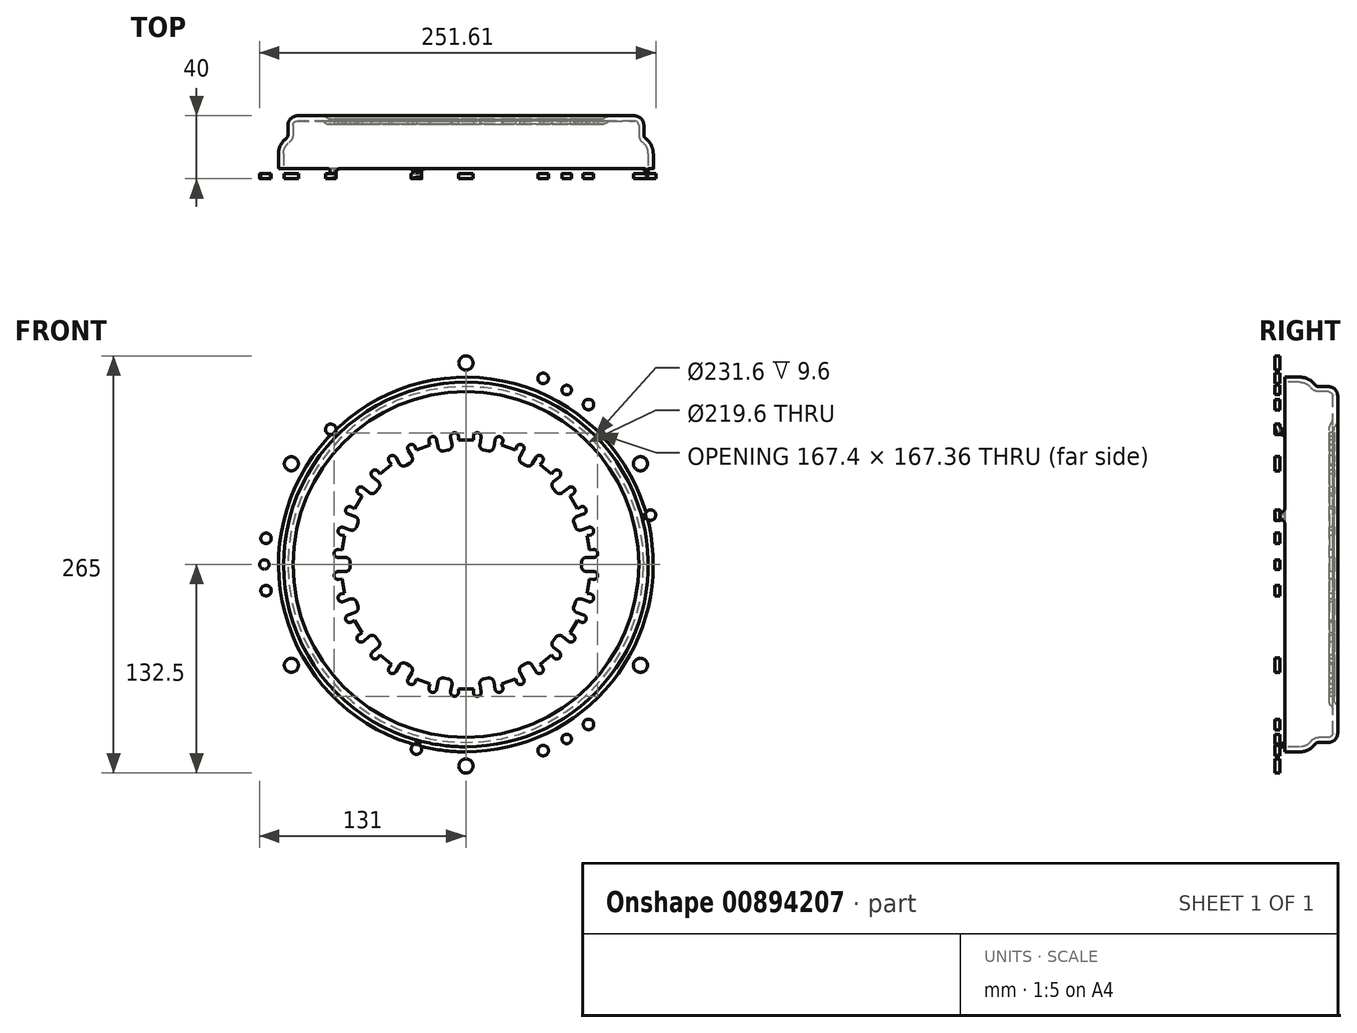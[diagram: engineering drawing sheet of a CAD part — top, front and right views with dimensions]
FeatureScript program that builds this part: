
annotation { "Feature Type Name" : "Feature", "Feature Type Description" : "" }
export const myFeature = defineFeature(function(context is Context, id is Id, definition is map)
    precondition{}
    {
        {
            var Q0;
            Q0=qCreatedBy(makeId("Right.planeOp"),FACE);
            var sketch = newSketch(context, id + "F0", { "sketchPlane" : qUnion([Q0])});
            skLineSegment(sketch, "E0", {"start": v(0, 136.5) * mm, "end": v(3.2, 136.5) * mm});
            skLineSegment(sketch, "E1", {"start": v(3.2, 136.5) * mm, "end": v(3.2, 121.5) * mm});
            skArc(sketch, "E2", {"start": v(3.2, 121.5) * mm, "mid": v(3.93, 119.73) * mm, "end": v(5.7, 119) * mm});
            skLineSegment(sketch, "E3", {"start": v(5.7, 119) * mm, "end": v(16, 119) * mm});
            skLineSegment(sketch, "E4", {"start": v(40, 107) * mm, "end": v(40, 91.97) * mm});
            skArc(sketch, "E5", {"start": v(38.15, 87.64) * mm, "mid": v(39.52, 89.62) * mm, "end": v(40, 91.97) * mm});
            skArc(sketch, "E6", {"start": v(38.15, 87.64) * mm, "mid": v(38.04, 87.48) * mm, "end": v(38, 87.28) * mm});
            skLineSegment(sketch, "E7", {"start": v(38, 87.28) * mm, "end": v(38, 73.5) * mm});
            skLineSegment(sketch, "E8", {"start": v(38, 73.5) * mm, "end": v(34.8, 73.5) * mm});
            skLineSegment(sketch, "E9", {"start": v(34, 113) * mm, "end": v(28, 113) * mm});
            skArc(sketch, "E10", {"start": v(40, 107) * mm, "mid": v(38.24, 111.24) * mm, "end": v(34, 113) * mm});
            skArc(sketch, "E11", {"start": v(25.6, 114.2) * mm, "mid": v(26.66, 113.32) * mm, "end": v(28, 113) * mm});
            skArc(sketch, "E12", {"start": v(25.6, 114.2) * mm, "mid": v(21.37, 117.73) * mm, "end": v(16, 119) * mm});
            skLineSegment(sketch, "E13", {"start": v(34.8, 73.5) * mm, "end": v(34.8, 87.28) * mm});
            skArc(sketch, "E14", {"start": v(35.94, 89.95) * mm, "mid": v(35.1, 88.73) * mm, "end": v(34.8, 87.28) * mm});
            skArc(sketch, "E15", {"start": v(35.94, 89.95) * mm, "mid": v(36.58, 90.87) * mm, "end": v(36.8, 91.97) * mm});
            skLineSegment(sketch, "E16", {"start": v(36.8, 91.97) * mm, "end": v(36.8, 107) * mm});
            skArc(sketch, "E17", {"start": v(36.8, 107) * mm, "mid": v(35.98, 108.98) * mm, "end": v(34, 109.8) * mm});
            skLineSegment(sketch, "E18", {"start": v(34, 109.8) * mm, "end": v(28, 109.8) * mm});
            skArc(sketch, "E19", {"start": v(23.04, 112.28) * mm, "mid": v(25.23, 110.45) * mm, "end": v(28, 109.8) * mm});
            skArc(sketch, "E20", {"start": v(23.04, 112.28) * mm, "mid": v(19.94, 114.87) * mm, "end": v(16, 115.8) * mm});
            skLineSegment(sketch, "E21", {"start": v(16, 115.8) * mm, "end": v(5.7, 115.8) * mm});
            skArc(sketch, "E22", {"start": v(0, 121.5) * mm, "mid": v(1.67, 117.47) * mm, "end": v(5.7, 115.8) * mm});
            skLineSegment(sketch, "E23", {"start": v(0, 0) * mm, "end": v(40, 0) * mm});
            skLineSegment(sketch, "E24", {"start": v(0, 136.5) * mm, "end": v(0, 121.5) * mm});
            skLineSegment(sketch, "E25", {"start": v(0, 121.5) * mm, "end": v(0, 0) * mm, "construction": true});
            skSolve(sketch);
        }
        {
            var Q0;
            Q0=makeQuery(id+"F0.imprint","IMPRINT",FACE,{"disambiguationData":[TD([[makeQuery(id+"F0.imprint","IMPRINT",EDGE,{"derivedFrom":sQuery(id+"F0.wireOp",EDGE,"E0")}),-1.0]])]});
            var Q1;
            Q1=sQuery(id+"F0.wireOp",EDGE,"E23");
            revolve(context, id + "F1", {"surfaceOperationType" : NewSurfaceOperationType.NEW, "entities" : qUnion([Q0]), "axis" : qUnion([Q1]), "revolveType" : RevolveType.FULL});
        }
        {
            var Q0;
            Q0=makeQuery(id+"F1.opRevolve","SWEPT_FACE",FACE,{"disambiguationData":[OSD([sQuery(id+"F0.wireOp",EDGE,"E24")])]});
            var sketch = newSketch(context, id + "F2", { "sketchPlane" : qUnion([Q0])});
            skLineSegment(sketch, "E26", {"start": v(18.53, 79.2) * mm, "end": v(17.72, 74.56) * mm});
            skArc(sketch, "E27", {"start": v(14.24, 72.12) * mm, "mid": v(16.48, 72.62) * mm, "end": v(17.72, 74.56) * mm});
            skLineSegment(sketch, "E28", {"start": v(9.67, 80.76) * mm, "end": v(8.85, 76.12) * mm});
            skLineSegment(sketch, "E29", {"start": v(12.76, 72.38) * mm, "end": v(14.24, 72.12) * mm});
            skLineSegment(sketch, "E30", {"start": v(12.76, 72.38) * mm, "end": v(11.29, 72.64) * mm});
            skArc(sketch, "E31", {"start": v(8.85, 76.12) * mm, "mid": v(9.35, 73.88) * mm, "end": v(11.29, 72.64) * mm});
            skLineSegment(sketch, "E32", {"start": v(4.7, 81.19) * mm, "end": v(4.7, 79) * mm});
            skLineSegment(sketch, "E33", {"start": v(0, 79) * mm, "end": v(4.7, 79) * mm});
            skLineSegment(sketch, "E34", {"start": v(23.34, 77.9) * mm, "end": v(22.6, 75.85) * mm});
            skLineSegment(sketch, "E35", {"start": v(27.02, 74.24) * mm, "end": v(22.6, 75.85) * mm});
            skArc(sketch, "E36", {"start": v(9.67, 80.76) * mm, "mid": v(7.43, 83.68) * mm, "end": v(4.7, 81.19) * mm});
            skArc(sketch, "E37", {"start": v(23.34, 77.9) * mm, "mid": v(21.64, 81.17) * mm, "end": v(18.53, 79.2) * mm});
            skLineSegment(sketch, "E38", {"start": v(0, 0) * mm, "end": v(0, 79) * mm, "construction": true});
            skCircle(sketch, "E39", {"center": v(0, 0) * mm, "radius": 81.5 * mm, "construction": true});
            skCircle(sketch, "E40", {"center": v(0, 0) * mm, "radius": 76.51 * mm, "construction": true});
            skLineSegment(sketch, "E41.1.0", {"start": v(-27.02, 74.24) * mm, "end": v(-22.6, 75.85) * mm});
            skLineSegment(sketch, "E41.1.1", {"start": v(-23.34, 77.9) * mm, "end": v(-22.6, 75.85) * mm});
            skArc(sketch, "E41.1.2", {"start": v(-18.53, 79.2) * mm, "mid": v(-21.64, 81.17) * mm, "end": v(-23.34, 77.9) * mm});
            skLineSegment(sketch, "E41.1.3", {"start": v(-18.53, 79.2) * mm, "end": v(-17.72, 74.56) * mm});
            skArc(sketch, "E41.1.4", {"start": v(-17.72, 74.56) * mm, "mid": v(-16.48, 72.62) * mm, "end": v(-14.24, 72.12) * mm});
            skLineSegment(sketch, "E41.1.5", {"start": v(-12.76, 72.38) * mm, "end": v(-14.24, 72.12) * mm});
            skLineSegment(sketch, "E41.1.6", {"start": v(-12.76, 72.38) * mm, "end": v(-11.29, 72.64) * mm});
            skArc(sketch, "E41.1.7", {"start": v(-11.29, 72.64) * mm, "mid": v(-9.35, 73.88) * mm, "end": v(-8.85, 76.12) * mm});
            skLineSegment(sketch, "E41.1.8", {"start": v(-9.67, 80.76) * mm, "end": v(-8.85, 76.12) * mm});
            skArc(sketch, "E41.1.9", {"start": v(-4.7, 81.19) * mm, "mid": v(-7.43, 83.68) * mm, "end": v(-9.67, 80.76) * mm});
            skLineSegment(sketch, "E41.1.10", {"start": v(-4.7, 81.19) * mm, "end": v(-4.7, 79) * mm});
            skLineSegment(sketch, "E41.1.11", {"start": v(0, 79) * mm, "end": v(-4.7, 79) * mm});
            skLineSegment(sketch, "E41.2.0", {"start": v(-50.78, 60.52) * mm, "end": v(-47.17, 63.54) * mm});
            skLineSegment(sketch, "E41.2.1", {"start": v(-48.58, 65.22) * mm, "end": v(-47.17, 63.54) * mm});
            skArc(sketch, "E41.2.2", {"start": v(-44.5, 68.08) * mm, "mid": v(-48.1, 68.88) * mm, "end": v(-48.58, 65.22) * mm});
            skLineSegment(sketch, "E41.2.3", {"start": v(-44.5, 68.08) * mm, "end": v(-42.15, 64) * mm});
            skArc(sketch, "E41.2.4", {"start": v(-42.15, 64) * mm, "mid": v(-40.33, 62.6) * mm, "end": v(-38.05, 62.9) * mm});
            skLineSegment(sketch, "E41.2.5", {"start": v(-36.75, 63.65) * mm, "end": v(-38.05, 62.9) * mm});
            skLineSegment(sketch, "E41.2.6", {"start": v(-36.75, 63.65) * mm, "end": v(-35.45, 64.4) * mm});
            skArc(sketch, "E41.2.7", {"start": v(-35.45, 64.4) * mm, "mid": v(-34.05, 66.22) * mm, "end": v(-34.35, 68.5) * mm});
            skLineSegment(sketch, "E41.2.8", {"start": v(-36.7, 72.58) * mm, "end": v(-34.35, 68.5) * mm});
            skArc(sketch, "E41.2.9", {"start": v(-32.2, 74.68) * mm, "mid": v(-35.6, 76.1) * mm, "end": v(-36.7, 72.58) * mm});
            skLineSegment(sketch, "E41.2.10", {"start": v(-32.2, 74.68) * mm, "end": v(-31.44, 72.63) * mm});
            skLineSegment(sketch, "E41.2.11", {"start": v(-27.02, 74.24) * mm, "end": v(-31.44, 72.63) * mm});
            skLineSegment(sketch, "E41.3.0", {"start": v(-68.42, 39.5) * mm, "end": v(-66.06, 43.58) * mm});
            skLineSegment(sketch, "E41.3.1", {"start": v(-67.96, 44.67) * mm, "end": v(-66.06, 43.58) * mm});
            skArc(sketch, "E41.3.2", {"start": v(-65.1, 48.75) * mm, "mid": v(-68.76, 48.27) * mm, "end": v(-67.96, 44.67) * mm});
            skLineSegment(sketch, "E41.3.3", {"start": v(-65.1, 48.75) * mm, "end": v(-61.5, 45.73) * mm});
            skArc(sketch, "E41.3.4", {"start": v(-61.5, 45.73) * mm, "mid": v(-59.3, 45.04) * mm, "end": v(-57.27, 46.1) * mm});
            skLineSegment(sketch, "E41.3.5", {"start": v(-56.3, 47.24) * mm, "end": v(-57.27, 46.1) * mm});
            skLineSegment(sketch, "E41.3.6", {"start": v(-56.3, 47.24) * mm, "end": v(-55.34, 48.4) * mm});
            skArc(sketch, "E41.3.7", {"start": v(-55.34, 48.4) * mm, "mid": v(-54.65, 50.58) * mm, "end": v(-55.7, 52.62) * mm});
            skLineSegment(sketch, "E41.3.8", {"start": v(-59.32, 55.65) * mm, "end": v(-55.7, 52.62) * mm});
            skArc(sketch, "E41.3.9", {"start": v(-55.8, 59.17) * mm, "mid": v(-59.48, 59.33) * mm, "end": v(-59.32, 55.65) * mm});
            skLineSegment(sketch, "E41.3.10", {"start": v(-55.8, 59.17) * mm, "end": v(-54.39, 57.5) * mm});
            skLineSegment(sketch, "E41.3.11", {"start": v(-50.78, 60.52) * mm, "end": v(-54.39, 57.5) * mm});
            skLineSegment(sketch, "E41.4.0", {"start": v(-77.8, 13.72) * mm, "end": v(-76.98, 18.35) * mm});
            skLineSegment(sketch, "E41.4.1", {"start": v(-79.14, 18.73) * mm, "end": v(-76.98, 18.35) * mm});
            skArc(sketch, "E41.4.2", {"start": v(-77.85, 23.55) * mm, "mid": v(-81.12, 21.84) * mm, "end": v(-79.14, 18.73) * mm});
            skLineSegment(sketch, "E41.4.3", {"start": v(-77.85, 23.55) * mm, "end": v(-73.43, 21.94) * mm});
            skArc(sketch, "E41.4.4", {"start": v(-73.43, 21.94) * mm, "mid": v(-71.13, 22.04) * mm, "end": v(-69.58, 23.73) * mm});
            skLineSegment(sketch, "E41.4.5", {"start": v(-69.07, 25.14) * mm, "end": v(-69.58, 23.73) * mm});
            skLineSegment(sketch, "E41.4.6", {"start": v(-69.07, 25.14) * mm, "end": v(-68.55, 26.55) * mm});
            skArc(sketch, "E41.4.7", {"start": v(-68.55, 26.55) * mm, "mid": v(-68.65, 28.84) * mm, "end": v(-70.35, 30.4) * mm});
            skLineSegment(sketch, "E41.4.8", {"start": v(-74.77, 32) * mm, "end": v(-70.35, 30.4) * mm});
            skArc(sketch, "E41.4.9", {"start": v(-72.67, 36.52) * mm, "mid": v(-76.18, 35.4) * mm, "end": v(-74.77, 32) * mm});
            skLineSegment(sketch, "E41.4.10", {"start": v(-72.67, 36.52) * mm, "end": v(-70.77, 35.42) * mm});
            skLineSegment(sketch, "E41.4.11", {"start": v(-68.42, 39.5) * mm, "end": v(-70.77, 35.42) * mm});
            skLineSegment(sketch, "E41.5.0", {"start": v(-77.8, -13.72) * mm, "end": v(-78.62, -9.08) * mm});
            skLineSegment(sketch, "E41.5.1", {"start": v(-80.77, -9.46) * mm, "end": v(-78.62, -9.08) * mm});
            skArc(sketch, "E41.5.2", {"start": v(-81.2, -4.5) * mm, "mid": v(-83.7, -7.22) * mm, "end": v(-80.77, -9.46) * mm});
            skLineSegment(sketch, "E41.5.3", {"start": v(-81.2, -4.5) * mm, "end": v(-76.5, -4.5) * mm});
            skArc(sketch, "E41.5.4", {"start": v(-76.5, -4.5) * mm, "mid": v(-74.38, -3.62) * mm, "end": v(-73.5, -1.5) * mm});
            skLineSegment(sketch, "E41.5.5", {"start": v(-73.5, 0) * mm, "end": v(-73.5, -1.5) * mm});
            skLineSegment(sketch, "E41.5.6", {"start": v(-73.5, 0) * mm, "end": v(-73.5, 1.5) * mm});
            skArc(sketch, "E41.5.7", {"start": v(-73.5, 1.5) * mm, "mid": v(-74.38, 3.62) * mm, "end": v(-76.5, 4.5) * mm});
            skLineSegment(sketch, "E41.5.8", {"start": v(-81.2, 4.5) * mm, "end": v(-76.5, 4.5) * mm});
            skArc(sketch, "E41.5.9", {"start": v(-80.77, 9.46) * mm, "mid": v(-83.7, 7.22) * mm, "end": v(-81.2, 4.5) * mm});
            skLineSegment(sketch, "E41.5.10", {"start": v(-80.77, 9.46) * mm, "end": v(-78.62, 9.08) * mm});
            skLineSegment(sketch, "E41.5.11", {"start": v(-77.8, 13.72) * mm, "end": v(-78.62, 9.08) * mm});
            skLineSegment(sketch, "E41.6.0", {"start": v(-68.42, -39.5) * mm, "end": v(-70.77, -35.42) * mm});
            skLineSegment(sketch, "E41.6.1", {"start": v(-72.67, -36.52) * mm, "end": v(-70.77, -35.42) * mm});
            skArc(sketch, "E41.6.2", {"start": v(-74.77, -32) * mm, "mid": v(-76.18, -35.4) * mm, "end": v(-72.67, -36.52) * mm});
            skLineSegment(sketch, "E41.6.3", {"start": v(-74.77, -32) * mm, "end": v(-70.35, -30.4) * mm});
            skArc(sketch, "E41.6.4", {"start": v(-70.35, -30.4) * mm, "mid": v(-68.65, -28.84) * mm, "end": v(-68.55, -26.55) * mm});
            skLineSegment(sketch, "E41.6.5", {"start": v(-69.07, -25.14) * mm, "end": v(-68.55, -26.55) * mm});
            skLineSegment(sketch, "E41.6.6", {"start": v(-69.07, -25.14) * mm, "end": v(-69.58, -23.73) * mm});
            skArc(sketch, "E41.6.7", {"start": v(-69.58, -23.73) * mm, "mid": v(-71.13, -22.04) * mm, "end": v(-73.43, -21.94) * mm});
            skLineSegment(sketch, "E41.6.8", {"start": v(-77.85, -23.55) * mm, "end": v(-73.43, -21.94) * mm});
            skArc(sketch, "E41.6.9", {"start": v(-79.14, -18.73) * mm, "mid": v(-81.12, -21.84) * mm, "end": v(-77.85, -23.55) * mm});
            skLineSegment(sketch, "E41.6.10", {"start": v(-79.14, -18.73) * mm, "end": v(-76.98, -18.35) * mm});
            skLineSegment(sketch, "E41.6.11", {"start": v(-77.8, -13.72) * mm, "end": v(-76.98, -18.35) * mm});
            skLineSegment(sketch, "E41.7.0", {"start": v(-50.78, -60.52) * mm, "end": v(-54.39, -57.5) * mm});
            skLineSegment(sketch, "E41.7.1", {"start": v(-55.8, -59.17) * mm, "end": v(-54.39, -57.5) * mm});
            skArc(sketch, "E41.7.2", {"start": v(-59.32, -55.65) * mm, "mid": v(-59.48, -59.33) * mm, "end": v(-55.8, -59.17) * mm});
            skLineSegment(sketch, "E41.7.3", {"start": v(-59.32, -55.65) * mm, "end": v(-55.7, -52.62) * mm});
            skArc(sketch, "E41.7.4", {"start": v(-55.7, -52.62) * mm, "mid": v(-54.65, -50.58) * mm, "end": v(-55.34, -48.4) * mm});
            skLineSegment(sketch, "E41.7.5", {"start": v(-56.3, -47.24) * mm, "end": v(-55.34, -48.4) * mm});
            skLineSegment(sketch, "E41.7.6", {"start": v(-56.3, -47.24) * mm, "end": v(-57.27, -46.1) * mm});
            skArc(sketch, "E41.7.7", {"start": v(-57.27, -46.1) * mm, "mid": v(-59.3, -45.04) * mm, "end": v(-61.5, -45.73) * mm});
            skLineSegment(sketch, "E41.7.8", {"start": v(-65.1, -48.75) * mm, "end": v(-61.5, -45.73) * mm});
            skArc(sketch, "E41.7.9", {"start": v(-67.96, -44.67) * mm, "mid": v(-68.76, -48.27) * mm, "end": v(-65.1, -48.75) * mm});
            skLineSegment(sketch, "E41.7.10", {"start": v(-67.96, -44.67) * mm, "end": v(-66.06, -43.58) * mm});
            skLineSegment(sketch, "E41.7.11", {"start": v(-68.42, -39.5) * mm, "end": v(-66.06, -43.58) * mm});
            skLineSegment(sketch, "E41.8.0", {"start": v(-27.02, -74.24) * mm, "end": v(-31.44, -72.63) * mm});
            skLineSegment(sketch, "E41.8.1", {"start": v(-32.2, -74.68) * mm, "end": v(-31.44, -72.63) * mm});
            skArc(sketch, "E41.8.2", {"start": v(-36.7, -72.58) * mm, "mid": v(-35.6, -76.1) * mm, "end": v(-32.2, -74.68) * mm});
            skLineSegment(sketch, "E41.8.3", {"start": v(-36.7, -72.58) * mm, "end": v(-34.35, -68.5) * mm});
            skArc(sketch, "E41.8.4", {"start": v(-34.35, -68.5) * mm, "mid": v(-34.05, -66.22) * mm, "end": v(-35.45, -64.4) * mm});
            skLineSegment(sketch, "E41.8.5", {"start": v(-36.75, -63.65) * mm, "end": v(-35.45, -64.4) * mm});
            skLineSegment(sketch, "E41.8.6", {"start": v(-36.75, -63.65) * mm, "end": v(-38.05, -62.9) * mm});
            skArc(sketch, "E41.8.7", {"start": v(-38.05, -62.9) * mm, "mid": v(-40.33, -62.6) * mm, "end": v(-42.15, -64) * mm});
            skLineSegment(sketch, "E41.8.8", {"start": v(-44.5, -68.08) * mm, "end": v(-42.15, -64) * mm});
            skArc(sketch, "E41.8.9", {"start": v(-48.58, -65.22) * mm, "mid": v(-48.1, -68.88) * mm, "end": v(-44.5, -68.08) * mm});
            skLineSegment(sketch, "E41.8.10", {"start": v(-48.58, -65.22) * mm, "end": v(-47.17, -63.54) * mm});
            skLineSegment(sketch, "E41.8.11", {"start": v(-50.78, -60.52) * mm, "end": v(-47.17, -63.54) * mm});
            skLineSegment(sketch, "E41.9.0", {"start": v(0, -79) * mm, "end": v(-4.7, -79) * mm});
            skLineSegment(sketch, "E41.9.1", {"start": v(-4.7, -81.19) * mm, "end": v(-4.7, -79) * mm});
            skArc(sketch, "E41.9.2", {"start": v(-9.67, -80.76) * mm, "mid": v(-7.43, -83.68) * mm, "end": v(-4.7, -81.19) * mm});
            skLineSegment(sketch, "E41.9.3", {"start": v(-9.67, -80.76) * mm, "end": v(-8.85, -76.12) * mm});
            skArc(sketch, "E41.9.4", {"start": v(-8.85, -76.12) * mm, "mid": v(-9.35, -73.88) * mm, "end": v(-11.29, -72.64) * mm});
            skLineSegment(sketch, "E41.9.5", {"start": v(-12.76, -72.38) * mm, "end": v(-11.29, -72.64) * mm});
            skLineSegment(sketch, "E41.9.6", {"start": v(-12.76, -72.38) * mm, "end": v(-14.24, -72.12) * mm});
            skArc(sketch, "E41.9.7", {"start": v(-14.24, -72.12) * mm, "mid": v(-16.48, -72.62) * mm, "end": v(-17.72, -74.56) * mm});
            skLineSegment(sketch, "E41.9.8", {"start": v(-18.53, -79.2) * mm, "end": v(-17.72, -74.56) * mm});
            skArc(sketch, "E41.9.9", {"start": v(-23.34, -77.9) * mm, "mid": v(-21.64, -81.17) * mm, "end": v(-18.53, -79.2) * mm});
            skLineSegment(sketch, "E41.9.10", {"start": v(-23.34, -77.9) * mm, "end": v(-22.6, -75.85) * mm});
            skLineSegment(sketch, "E41.9.11", {"start": v(-27.02, -74.24) * mm, "end": v(-22.6, -75.85) * mm});
            skLineSegment(sketch, "E41.10.0", {"start": v(27.02, -74.24) * mm, "end": v(22.6, -75.85) * mm});
            skLineSegment(sketch, "E41.10.1", {"start": v(23.34, -77.9) * mm, "end": v(22.6, -75.85) * mm});
            skArc(sketch, "E41.10.2", {"start": v(18.53, -79.2) * mm, "mid": v(21.64, -81.17) * mm, "end": v(23.34, -77.9) * mm});
            skLineSegment(sketch, "E41.10.3", {"start": v(18.53, -79.2) * mm, "end": v(17.72, -74.56) * mm});
            skArc(sketch, "E41.10.4", {"start": v(17.72, -74.56) * mm, "mid": v(16.48, -72.62) * mm, "end": v(14.24, -72.12) * mm});
            skLineSegment(sketch, "E41.10.5", {"start": v(12.76, -72.38) * mm, "end": v(14.24, -72.12) * mm});
            skLineSegment(sketch, "E41.10.6", {"start": v(12.76, -72.38) * mm, "end": v(11.29, -72.64) * mm});
            skArc(sketch, "E41.10.7", {"start": v(11.29, -72.64) * mm, "mid": v(9.35, -73.88) * mm, "end": v(8.85, -76.12) * mm});
            skLineSegment(sketch, "E41.10.8", {"start": v(9.67, -80.76) * mm, "end": v(8.85, -76.12) * mm});
            skArc(sketch, "E41.10.9", {"start": v(4.7, -81.19) * mm, "mid": v(7.43, -83.68) * mm, "end": v(9.67, -80.76) * mm});
            skLineSegment(sketch, "E41.10.10", {"start": v(4.7, -81.19) * mm, "end": v(4.7, -79) * mm});
            skLineSegment(sketch, "E41.10.11", {"start": v(0, -79) * mm, "end": v(4.7, -79) * mm});
            skLineSegment(sketch, "E41.11.0", {"start": v(50.78, -60.52) * mm, "end": v(47.17, -63.54) * mm});
            skLineSegment(sketch, "E41.11.1", {"start": v(48.58, -65.22) * mm, "end": v(47.17, -63.54) * mm});
            skArc(sketch, "E41.11.2", {"start": v(44.5, -68.08) * mm, "mid": v(48.1, -68.88) * mm, "end": v(48.58, -65.22) * mm});
            skLineSegment(sketch, "E41.11.3", {"start": v(44.5, -68.08) * mm, "end": v(42.15, -64) * mm});
            skArc(sketch, "E41.11.4", {"start": v(42.15, -64) * mm, "mid": v(40.33, -62.6) * mm, "end": v(38.05, -62.9) * mm});
            skLineSegment(sketch, "E41.11.5", {"start": v(36.75, -63.65) * mm, "end": v(38.05, -62.9) * mm});
            skLineSegment(sketch, "E41.11.6", {"start": v(36.75, -63.65) * mm, "end": v(35.45, -64.4) * mm});
            skArc(sketch, "E41.11.7", {"start": v(35.45, -64.4) * mm, "mid": v(34.05, -66.22) * mm, "end": v(34.35, -68.5) * mm});
            skLineSegment(sketch, "E41.11.8", {"start": v(36.7, -72.58) * mm, "end": v(34.35, -68.5) * mm});
            skArc(sketch, "E41.11.9", {"start": v(32.2, -74.68) * mm, "mid": v(35.6, -76.1) * mm, "end": v(36.7, -72.58) * mm});
            skLineSegment(sketch, "E41.11.10", {"start": v(32.2, -74.68) * mm, "end": v(31.44, -72.63) * mm});
            skLineSegment(sketch, "E41.11.11", {"start": v(27.02, -74.24) * mm, "end": v(31.44, -72.63) * mm});
            skLineSegment(sketch, "E41.12.0", {"start": v(68.42, -39.5) * mm, "end": v(66.06, -43.58) * mm});
            skLineSegment(sketch, "E41.12.1", {"start": v(67.96, -44.67) * mm, "end": v(66.06, -43.58) * mm});
            skArc(sketch, "E41.12.2", {"start": v(65.1, -48.75) * mm, "mid": v(68.76, -48.27) * mm, "end": v(67.96, -44.67) * mm});
            skLineSegment(sketch, "E41.12.3", {"start": v(65.1, -48.75) * mm, "end": v(61.5, -45.73) * mm});
            skArc(sketch, "E41.12.4", {"start": v(61.5, -45.73) * mm, "mid": v(59.3, -45.04) * mm, "end": v(57.27, -46.1) * mm});
            skLineSegment(sketch, "E41.12.5", {"start": v(56.3, -47.24) * mm, "end": v(57.27, -46.1) * mm});
            skLineSegment(sketch, "E41.12.6", {"start": v(56.3, -47.24) * mm, "end": v(55.34, -48.4) * mm});
            skArc(sketch, "E41.12.7", {"start": v(55.34, -48.4) * mm, "mid": v(54.65, -50.58) * mm, "end": v(55.7, -52.62) * mm});
            skLineSegment(sketch, "E41.12.8", {"start": v(59.32, -55.65) * mm, "end": v(55.7, -52.62) * mm});
            skArc(sketch, "E41.12.9", {"start": v(55.8, -59.17) * mm, "mid": v(59.48, -59.33) * mm, "end": v(59.32, -55.65) * mm});
            skLineSegment(sketch, "E41.12.10", {"start": v(55.8, -59.17) * mm, "end": v(54.39, -57.5) * mm});
            skLineSegment(sketch, "E41.12.11", {"start": v(50.78, -60.52) * mm, "end": v(54.39, -57.5) * mm});
            skLineSegment(sketch, "E41.13.0", {"start": v(77.8, -13.72) * mm, "end": v(76.98, -18.35) * mm});
            skLineSegment(sketch, "E41.13.1", {"start": v(79.14, -18.73) * mm, "end": v(76.98, -18.35) * mm});
            skArc(sketch, "E41.13.2", {"start": v(77.85, -23.55) * mm, "mid": v(81.12, -21.84) * mm, "end": v(79.14, -18.73) * mm});
            skLineSegment(sketch, "E41.13.3", {"start": v(77.85, -23.55) * mm, "end": v(73.43, -21.94) * mm});
            skArc(sketch, "E41.13.4", {"start": v(73.43, -21.94) * mm, "mid": v(71.13, -22.04) * mm, "end": v(69.58, -23.73) * mm});
            skLineSegment(sketch, "E41.13.5", {"start": v(69.07, -25.14) * mm, "end": v(69.58, -23.73) * mm});
            skLineSegment(sketch, "E41.13.6", {"start": v(69.07, -25.14) * mm, "end": v(68.55, -26.55) * mm});
            skArc(sketch, "E41.13.7", {"start": v(68.55, -26.55) * mm, "mid": v(68.65, -28.84) * mm, "end": v(70.35, -30.4) * mm});
            skLineSegment(sketch, "E41.13.8", {"start": v(74.77, -32) * mm, "end": v(70.35, -30.4) * mm});
            skArc(sketch, "E41.13.9", {"start": v(72.67, -36.52) * mm, "mid": v(76.18, -35.4) * mm, "end": v(74.77, -32) * mm});
            skLineSegment(sketch, "E41.13.10", {"start": v(72.67, -36.52) * mm, "end": v(70.77, -35.42) * mm});
            skLineSegment(sketch, "E41.13.11", {"start": v(68.42, -39.5) * mm, "end": v(70.77, -35.42) * mm});
            skLineSegment(sketch, "E41.14.0", {"start": v(77.8, 13.72) * mm, "end": v(78.62, 9.08) * mm});
            skLineSegment(sketch, "E41.14.1", {"start": v(80.77, 9.46) * mm, "end": v(78.62, 9.08) * mm});
            skArc(sketch, "E41.14.2", {"start": v(81.2, 4.5) * mm, "mid": v(83.7, 7.22) * mm, "end": v(80.77, 9.46) * mm});
            skLineSegment(sketch, "E41.14.3", {"start": v(81.2, 4.5) * mm, "end": v(76.5, 4.5) * mm});
            skArc(sketch, "E41.14.4", {"start": v(76.5, 4.5) * mm, "mid": v(74.38, 3.62) * mm, "end": v(73.5, 1.5) * mm});
            skLineSegment(sketch, "E41.14.5", {"start": v(73.5, 0) * mm, "end": v(73.5, 1.5) * mm});
            skLineSegment(sketch, "E41.14.6", {"start": v(73.5, 0) * mm, "end": v(73.5, -1.5) * mm});
            skArc(sketch, "E41.14.7", {"start": v(73.5, -1.5) * mm, "mid": v(74.38, -3.62) * mm, "end": v(76.5, -4.5) * mm});
            skLineSegment(sketch, "E41.14.8", {"start": v(81.2, -4.5) * mm, "end": v(76.5, -4.5) * mm});
            skArc(sketch, "E41.14.9", {"start": v(80.77, -9.46) * mm, "mid": v(83.7, -7.22) * mm, "end": v(81.2, -4.5) * mm});
            skLineSegment(sketch, "E41.14.10", {"start": v(80.77, -9.46) * mm, "end": v(78.62, -9.08) * mm});
            skLineSegment(sketch, "E41.14.11", {"start": v(77.8, -13.72) * mm, "end": v(78.62, -9.08) * mm});
            skLineSegment(sketch, "E41.15.0", {"start": v(68.42, 39.5) * mm, "end": v(70.77, 35.42) * mm});
            skLineSegment(sketch, "E41.15.1", {"start": v(72.67, 36.52) * mm, "end": v(70.77, 35.42) * mm});
            skArc(sketch, "E41.15.2", {"start": v(74.77, 32) * mm, "mid": v(76.18, 35.4) * mm, "end": v(72.67, 36.52) * mm});
            skLineSegment(sketch, "E41.15.3", {"start": v(74.77, 32) * mm, "end": v(70.35, 30.4) * mm});
            skArc(sketch, "E41.15.4", {"start": v(70.35, 30.4) * mm, "mid": v(68.65, 28.84) * mm, "end": v(68.55, 26.55) * mm});
            skLineSegment(sketch, "E41.15.5", {"start": v(69.07, 25.14) * mm, "end": v(68.55, 26.55) * mm});
            skLineSegment(sketch, "E41.15.6", {"start": v(69.07, 25.14) * mm, "end": v(69.58, 23.73) * mm});
            skArc(sketch, "E41.15.7", {"start": v(69.58, 23.73) * mm, "mid": v(71.13, 22.04) * mm, "end": v(73.43, 21.94) * mm});
            skLineSegment(sketch, "E41.15.8", {"start": v(77.85, 23.55) * mm, "end": v(73.43, 21.94) * mm});
            skArc(sketch, "E41.15.9", {"start": v(79.14, 18.73) * mm, "mid": v(81.12, 21.84) * mm, "end": v(77.85, 23.55) * mm});
            skLineSegment(sketch, "E41.15.10", {"start": v(79.14, 18.73) * mm, "end": v(76.98, 18.35) * mm});
            skLineSegment(sketch, "E41.15.11", {"start": v(77.8, 13.72) * mm, "end": v(76.98, 18.35) * mm});
            skLineSegment(sketch, "E41.16.0", {"start": v(50.78, 60.52) * mm, "end": v(54.39, 57.5) * mm});
            skLineSegment(sketch, "E41.16.1", {"start": v(55.8, 59.17) * mm, "end": v(54.39, 57.5) * mm});
            skArc(sketch, "E41.16.2", {"start": v(59.32, 55.65) * mm, "mid": v(59.48, 59.33) * mm, "end": v(55.8, 59.17) * mm});
            skLineSegment(sketch, "E41.16.3", {"start": v(59.32, 55.65) * mm, "end": v(55.7, 52.62) * mm});
            skArc(sketch, "E41.16.4", {"start": v(55.7, 52.62) * mm, "mid": v(54.65, 50.58) * mm, "end": v(55.34, 48.4) * mm});
            skLineSegment(sketch, "E41.16.5", {"start": v(56.3, 47.24) * mm, "end": v(55.34, 48.4) * mm});
            skLineSegment(sketch, "E41.16.6", {"start": v(56.3, 47.24) * mm, "end": v(57.27, 46.1) * mm});
            skArc(sketch, "E41.16.7", {"start": v(57.27, 46.1) * mm, "mid": v(59.3, 45.04) * mm, "end": v(61.5, 45.73) * mm});
            skLineSegment(sketch, "E41.16.8", {"start": v(65.1, 48.75) * mm, "end": v(61.5, 45.73) * mm});
            skArc(sketch, "E41.16.9", {"start": v(67.96, 44.67) * mm, "mid": v(68.76, 48.27) * mm, "end": v(65.1, 48.75) * mm});
            skLineSegment(sketch, "E41.16.10", {"start": v(67.96, 44.67) * mm, "end": v(66.06, 43.58) * mm});
            skLineSegment(sketch, "E41.16.11", {"start": v(68.42, 39.5) * mm, "end": v(66.06, 43.58) * mm});
            skLineSegment(sketch, "E41.17.0", {"start": v(27.02, 74.24) * mm, "end": v(31.44, 72.63) * mm});
            skLineSegment(sketch, "E41.17.1", {"start": v(32.2, 74.68) * mm, "end": v(31.44, 72.63) * mm});
            skArc(sketch, "E41.17.2", {"start": v(36.7, 72.58) * mm, "mid": v(35.6, 76.1) * mm, "end": v(32.2, 74.68) * mm});
            skLineSegment(sketch, "E41.17.3", {"start": v(36.7, 72.58) * mm, "end": v(34.35, 68.5) * mm});
            skArc(sketch, "E41.17.4", {"start": v(34.35, 68.5) * mm, "mid": v(34.05, 66.22) * mm, "end": v(35.45, 64.4) * mm});
            skLineSegment(sketch, "E41.17.5", {"start": v(36.75, 63.65) * mm, "end": v(35.45, 64.4) * mm});
            skLineSegment(sketch, "E41.17.6", {"start": v(36.75, 63.65) * mm, "end": v(38.05, 62.9) * mm});
            skArc(sketch, "E41.17.7", {"start": v(38.05, 62.9) * mm, "mid": v(40.33, 62.6) * mm, "end": v(42.15, 64) * mm});
            skLineSegment(sketch, "E41.17.8", {"start": v(44.5, 68.08) * mm, "end": v(42.15, 64) * mm});
            skArc(sketch, "E41.17.9", {"start": v(48.58, 65.22) * mm, "mid": v(48.1, 68.88) * mm, "end": v(44.5, 68.08) * mm});
            skLineSegment(sketch, "E41.17.10", {"start": v(48.58, 65.22) * mm, "end": v(47.17, 63.54) * mm});
            skLineSegment(sketch, "E41.17.11", {"start": v(50.78, 60.52) * mm, "end": v(47.17, 63.54) * mm});
            skCircle(sketch, "E42", {"center": v(0, 0) * mm, "radius": 70 * mm});
            skSolve(sketch);
        }
        {
            var Q0;
            Q0=makeQuery(id+"F2.imprint","IMPRINT",FACE,{"disambiguationData":[TD([[makeQuery(id+"F2.imprint","IMPRINT",EDGE,{"derivedFrom":sQuery(id+"F2.wireOp",EDGE,"E26")}),1.0]])]});
            extrude(context, id + "F3", {"entities" : qUnion([Q0]), "operationType" : NewBodyOperationType.REMOVE, "endBound" : BoundingType.THROUGH_ALL, "oppositeDirection" : true, "depth" : 25 * mm, "offsetDistance" : 25 * mm});
        }
        {
            var Q0;
            Q0=makeQuery(id+"F1.opRevolve","SWEPT_FACE",FACE,{"disambiguationData":[OSD([sQuery(id+"F0.wireOp",EDGE,"E24")])]});
            var sketch = newSketch(context, id + "F4", { "sketchPlane" : qUnion([Q0])});
            skArc(sketch, "E43", {"start": v(121.35, 62.5) * mm, "mid": v(68.25, 118.21) * mm, "end": v(-6.55, 136.34) * mm});
            skCircle(sketch, "E44", {"center": v(0, 128) * mm, "radius": 4.5 * mm});
            skCircle(sketch, "E45", {"center": v(-110.85, 64) * mm, "radius": 4.5 * mm});
            skCircle(sketch, "E46", {"center": v(64, 110.85) * mm, "radius": 3 * mm});
            skCircle(sketch, "E47", {"center": v(-85.84, 85.84) * mm, "radius": 3.35 * mm});
            skArc(sketch, "E48", {"start": v(-20.8, 125.03) * mm, "mid": v(-52.53, 115.35) * mm, "end": v(-80.66, 97.77) * mm});
            skArc(sketch, "E49", {"start": v(-83.02, 98.4) * mm, "mid": v(-91.34, 90.74) * mm, "end": v(-98.95, 82.38) * mm});
            skLineSegment(sketch, "E50", {"start": v(-114.8, 73.84) * mm, "end": v(-98.95, 82.38) * mm});
            skLineSegment(sketch, "E51", {"start": v(-6.55, 136.34) * mm, "end": v(-20.8, 125.03) * mm});
            skLineSegment(sketch, "E52", {"start": v(-83.02, 98.4) * mm, "end": v(-80.66, 97.77) * mm});
            skCircle(sketch, "E53", {"center": v(49.07, 118.22) * mm, "radius": 3.35 * mm});
            skCircle(sketch, "E54", {"center": v(77.85, 101.6) * mm, "radius": 3.35 * mm});
            skLineSegment(sketch, "E55", {"start": v(0, 0) * mm, "end": v(0, 136.5) * mm, "construction": true});
            skCircle(sketch, "E56", {"center": v(0, 0) * mm, "radius": 128 * mm, "construction": true});
            skLineSegment(sketch, "E57", {"start": v(49.07, 118.22) * mm, "end": v(0, 0) * mm, "construction": true});
            skLineSegment(sketch, "E58", {"start": v(64, 110.85) * mm, "end": v(0, 0) * mm, "construction": true});
            skLineSegment(sketch, "E59", {"start": v(77.85, 101.6) * mm, "end": v(0, 0) * mm, "construction": true});
            skLineSegment(sketch, "E60", {"start": v(-85.84, 85.84) * mm, "end": v(0, 0) * mm, "construction": true});
            skLineSegment(sketch, "E61", {"start": v(-110.85, 64) * mm, "end": v(0, 0) * mm, "construction": true});
            skCircle(sketch, "E62.1.0", {"center": v(0, -128) * mm, "radius": 4.5 * mm});
            skLineSegment(sketch, "E62.1.1", {"start": v(-6.55, -136.34) * mm, "end": v(-21.87, -126.88) * mm});
            skArc(sketch, "E62.1.2", {"start": v(-43.7, -121.1) * mm, "mid": v(-32.92, -124.47) * mm, "end": v(-21.87, -126.88) * mm});
            skLineSegment(sketch, "E62.1.3", {"start": v(-43.7, -121.1) * mm, "end": v(-44.34, -118.74) * mm});
            skArc(sketch, "E62.1.4", {"start": v(-97.88, -80.53) * mm, "mid": v(-73.63, -103.17) * mm, "end": v(-44.34, -118.74) * mm});
            skLineSegment(sketch, "E62.1.5", {"start": v(-114.8, -73.84) * mm, "end": v(-97.88, -80.53) * mm});
            skArc(sketch, "E62.1.6", {"start": v(-114.8, 73.84) * mm, "mid": v(-136.5, 0) * mm, "end": v(-114.8, -73.84) * mm});
            skCircle(sketch, "E62.1.7", {"center": v(-110.85, -64) * mm, "radius": 4.5 * mm});
            skCircle(sketch, "E62.1.8", {"center": v(-31.42, -117.26) * mm, "radius": 3.35 * mm});
            skCircle(sketch, "E62.1.9", {"center": v(-126.92, -16.61) * mm, "radius": 3.35 * mm});
            skCircle(sketch, "E62.1.10", {"center": v(-128, 0) * mm, "radius": 3 * mm});
            skCircle(sketch, "E62.1.11", {"center": v(-126.92, 16.61) * mm, "radius": 3.35 * mm});
            skCircle(sketch, "E62.2.0", {"center": v(110.85, 64) * mm, "radius": 4.5 * mm});
            skLineSegment(sketch, "E62.2.1", {"start": v(121.35, 62.5) * mm, "end": v(120.82, 44.5) * mm});
            skArc(sketch, "E62.2.2", {"start": v(126.73, 22.7) * mm, "mid": v(124.25, 33.73) * mm, "end": v(120.82, 44.5) * mm});
            skLineSegment(sketch, "E62.2.3", {"start": v(126.73, 22.7) * mm, "end": v(125, 20.97) * mm});
            skArc(sketch, "E62.2.4", {"start": v(118.68, -44.5) * mm, "mid": v(126.16, -12.18) * mm, "end": v(125, 20.97) * mm});
            skLineSegment(sketch, "E62.2.5", {"start": v(121.35, -62.5) * mm, "end": v(118.68, -44.5) * mm});
            skArc(sketch, "E62.2.6", {"start": v(-6.55, -136.34) * mm, "mid": v(68.25, -118.21) * mm, "end": v(121.35, -62.5) * mm});
            skCircle(sketch, "E62.2.7", {"center": v(110.85, -64) * mm, "radius": 4.5 * mm});
            skCircle(sketch, "E62.2.8", {"center": v(117.26, 31.42) * mm, "radius": 3.35 * mm});
            skCircle(sketch, "E62.2.9", {"center": v(77.85, -101.6) * mm, "radius": 3.35 * mm});
            skCircle(sketch, "E62.2.10", {"center": v(64, -110.85) * mm, "radius": 3 * mm});
            skCircle(sketch, "E62.2.11", {"center": v(49.07, -118.22) * mm, "radius": 3.35 * mm});
            skCircle(sketch, "E63", {"center": v(0, 0) * mm, "radius": 150 * mm});
            skSolve(sketch);
        }
        {
            var Q0;
            Q0=makeQuery(id+"F4.imprint","IMPRINT",FACE,{"disambiguationData":[TD([[makeQuery(id+"F4.imprint","IMPRINT",EDGE,{"derivedFrom":sQuery(id+"F4.wireOp",EDGE,"E44")}),-1.0]])]});
            var Q1;
            Q1=makeQuery(id+"F4.imprint","IMPRINT",FACE,{"disambiguationData":[TD([[makeQuery(id+"F4.imprint","IMPRINT",EDGE,{"derivedFrom":sQuery(id+"F4.wireOp",EDGE,"E53")}),-1.0]])]});
            var Q2;
            Q2=makeQuery(id+"F4.imprint","IMPRINT",FACE,{"disambiguationData":[TD([[makeQuery(id+"F4.imprint","IMPRINT",EDGE,{"derivedFrom":sQuery(id+"F4.wireOp",EDGE,"E46")}),-1.0]])]});
            var Q3;
            Q3=makeQuery(id+"F4.imprint","IMPRINT",FACE,{"disambiguationData":[TD([[makeQuery(id+"F4.imprint","IMPRINT",EDGE,{"derivedFrom":sQuery(id+"F4.wireOp",EDGE,"E54")}),-1.0]])]});
            var Q4;
            Q4=makeQuery(id+"F4.imprint","IMPRINT",FACE,{"disambiguationData":[TD([[makeQuery(id+"F4.imprint","IMPRINT",EDGE,{"derivedFrom":sQuery(id+"F4.wireOp",EDGE,"E62.2.0")}),-1.0]])]});
            var Q5;
            {var subQ0=sQuery(id+"F4.wireOp",EDGE,"E47");var subQ1=makeQuery(id+"F1.opRevolve","SWEPT_EDGE",EDGE,{"disambiguationData":[OSD([sQuery(id+"F0.wireOp",EDGE,"E22"),sQuery(id+"F0.wireOp",EDGE,"E24")])]});var subQ2=makeQuery(id+"F4.imprint","INTERSECT",VERTEX,{"disambiguationData":[OD(0.0)],"derivedFrom":[subQ1,subQ0]});Q5=makeQuery(id+"F4.imprint","IMPRINT",FACE,{"disambiguationData":[TD([[makeQuery(id+"F4.imprint","IMPRINT",EDGE,{"disambiguationData":[TD([[subQ2,-1.0]])],"derivedFrom":subQ0}),-1.0]])]});}
            var Q6;
            {var subQ0=sQuery(id+"F4.wireOp",EDGE,"E47");var subQ1=makeQuery(id+"F1.opRevolve","SWEPT_EDGE",EDGE,{"disambiguationData":[OSD([sQuery(id+"F0.wireOp",EDGE,"E22"),sQuery(id+"F0.wireOp",EDGE,"E24")])]});var subQ2=makeQuery(id+"F4.imprint","INTERSECT",VERTEX,{"disambiguationData":[OD(0.0)],"derivedFrom":[subQ1,subQ0]});Q6=makeQuery(id+"F4.imprint","IMPRINT",FACE,{"disambiguationData":[TD([[makeQuery(id+"F4.imprint","IMPRINT",EDGE,{"disambiguationData":[TD([[subQ2,1.0]])],"derivedFrom":subQ0}),-1.0]])]});}
            var Q7;
            Q7=makeQuery(id+"F4.imprint","IMPRINT",FACE,{"disambiguationData":[TD([[makeQuery(id+"F4.imprint","IMPRINT",EDGE,{"derivedFrom":sQuery(id+"F4.wireOp",EDGE,"E45")}),-1.0]])]});
            var Q8;
            Q8=makeQuery(id+"F4.imprint","IMPRINT",FACE,{"disambiguationData":[TD([[makeQuery(id+"F4.imprint","IMPRINT",EDGE,{"derivedFrom":sQuery(id+"F4.wireOp",EDGE,"E48")}),-1.0]])]});
            var Q9;
            {var subQ2=sQuery(id+"F4.wireOp",EDGE,"E43");Q9=makeQuery(id+"F4.imprint","IMPRINT",FACE,{"disambiguationData":[TD([[makeQuery(id+"F4.imprint","IMPRINT",EDGE,{"derivedFrom":subQ2}),-1.0]])]});}
            var Q10;
            Q10=makeQuery(id+"F4.imprint","IMPRINT",FACE,{"disambiguationData":[TD([[makeQuery(id+"F4.imprint","IMPRINT",EDGE,{"derivedFrom":sQuery(id+"F4.wireOp",EDGE,"E62.1.11")}),-1.0]])]});
            var Q11;
            Q11=makeQuery(id+"F4.imprint","IMPRINT",FACE,{"disambiguationData":[TD([[makeQuery(id+"F4.imprint","IMPRINT",EDGE,{"derivedFrom":sQuery(id+"F4.wireOp",EDGE,"E62.1.10")}),-1.0]])]});
            var Q12;
            Q12=makeQuery(id+"F4.imprint","IMPRINT",FACE,{"disambiguationData":[TD([[makeQuery(id+"F4.imprint","IMPRINT",EDGE,{"derivedFrom":sQuery(id+"F4.wireOp",EDGE,"E62.1.9")}),-1.0]])]});
            var Q13;
            Q13=makeQuery(id+"F4.imprint","IMPRINT",FACE,{"disambiguationData":[TD([[makeQuery(id+"F4.imprint","IMPRINT",EDGE,{"derivedFrom":sQuery(id+"F4.wireOp",EDGE,"E62.1.7")}),-1.0]])]});
            var Q14;
            {var subQ0=sQuery(id+"F4.wireOp",EDGE,"E62.1.1");Q14=makeQuery(id+"F4.imprint","IMPRINT",FACE,{"disambiguationData":[TD([[makeQuery(id+"F4.imprint","IMPRINT",EDGE,{"derivedFrom":subQ0}),1.0]])]});}
            var Q15;
            {var subQ0=sQuery(id+"F4.wireOp",EDGE,"E62.1.8");var subQ1=makeQuery(id+"F1.opRevolve","SWEPT_EDGE",EDGE,{"disambiguationData":[OSD([sQuery(id+"F0.wireOp",EDGE,"E22"),sQuery(id+"F0.wireOp",EDGE,"E24")])]});var subQ2=makeQuery(id+"F4.imprint","INTERSECT",VERTEX,{"disambiguationData":[OD(0.0)],"derivedFrom":[subQ1,subQ0]});Q15=makeQuery(id+"F4.imprint","IMPRINT",FACE,{"disambiguationData":[TD([[makeQuery(id+"F4.imprint","IMPRINT",EDGE,{"disambiguationData":[TD([[subQ2,1.0]])],"derivedFrom":subQ0}),-1.0]])]});}
            var Q16;
            {var subQ0=sQuery(id+"F4.wireOp",EDGE,"E62.1.8");var subQ1=makeQuery(id+"F1.opRevolve","SWEPT_EDGE",EDGE,{"disambiguationData":[OSD([sQuery(id+"F0.wireOp",EDGE,"E22"),sQuery(id+"F0.wireOp",EDGE,"E24")])]});var subQ2=makeQuery(id+"F4.imprint","INTERSECT",VERTEX,{"disambiguationData":[OD(0.0)],"derivedFrom":[subQ1,subQ0]});Q16=makeQuery(id+"F4.imprint","IMPRINT",FACE,{"disambiguationData":[TD([[makeQuery(id+"F4.imprint","IMPRINT",EDGE,{"disambiguationData":[TD([[subQ2,-1.0]])],"derivedFrom":subQ0}),-1.0]])]});}
            var Q17;
            Q17=makeQuery(id+"F4.imprint","IMPRINT",FACE,{"disambiguationData":[TD([[makeQuery(id+"F4.imprint","IMPRINT",EDGE,{"derivedFrom":sQuery(id+"F4.wireOp",EDGE,"E62.1.0")}),-1.0]])]});
            var Q18;
            Q18=makeQuery(id+"F4.imprint","IMPRINT",FACE,{"disambiguationData":[TD([[makeQuery(id+"F4.imprint","IMPRINT",EDGE,{"derivedFrom":sQuery(id+"F4.wireOp",EDGE,"E62.2.11")}),-1.0]])]});
            var Q19;
            Q19=makeQuery(id+"F4.imprint","IMPRINT",FACE,{"disambiguationData":[TD([[makeQuery(id+"F4.imprint","IMPRINT",EDGE,{"derivedFrom":sQuery(id+"F4.wireOp",EDGE,"E62.2.10")}),-1.0]])]});
            var Q20;
            Q20=makeQuery(id+"F4.imprint","IMPRINT",FACE,{"disambiguationData":[TD([[makeQuery(id+"F4.imprint","IMPRINT",EDGE,{"derivedFrom":sQuery(id+"F4.wireOp",EDGE,"E62.2.9")}),-1.0]])]});
            var Q21;
            Q21=makeQuery(id+"F4.imprint","IMPRINT",FACE,{"disambiguationData":[TD([[makeQuery(id+"F4.imprint","IMPRINT",EDGE,{"derivedFrom":sQuery(id+"F4.wireOp",EDGE,"E62.2.7")}),-1.0]])]});
            var Q22;
            {var subQ0=sQuery(id+"F4.wireOp",EDGE,"E62.2.1");Q22=makeQuery(id+"F4.imprint","IMPRINT",FACE,{"disambiguationData":[TD([[makeQuery(id+"F4.imprint","IMPRINT",EDGE,{"derivedFrom":subQ0}),1.0]])]});}
            var Q23;
            {var subQ0=sQuery(id+"F4.wireOp",EDGE,"E62.2.8");var subQ1=makeQuery(id+"F1.opRevolve","SWEPT_EDGE",EDGE,{"disambiguationData":[OSD([sQuery(id+"F0.wireOp",EDGE,"E22"),sQuery(id+"F0.wireOp",EDGE,"E24")])]});var subQ2=makeQuery(id+"F4.imprint","INTERSECT",VERTEX,{"disambiguationData":[OD(0.0)],"derivedFrom":[subQ1,subQ0]});Q23=makeQuery(id+"F4.imprint","IMPRINT",FACE,{"disambiguationData":[TD([[makeQuery(id+"F4.imprint","IMPRINT",EDGE,{"disambiguationData":[TD([[subQ2,1.0]])],"derivedFrom":subQ0}),-1.0]])]});}
            var Q24;
            {var subQ0=sQuery(id+"F4.wireOp",EDGE,"E62.2.8");var subQ1=makeQuery(id+"F1.opRevolve","SWEPT_EDGE",EDGE,{"disambiguationData":[OSD([sQuery(id+"F0.wireOp",EDGE,"E22"),sQuery(id+"F0.wireOp",EDGE,"E24")])]});var subQ2=makeQuery(id+"F4.imprint","INTERSECT",VERTEX,{"disambiguationData":[OD(0.0)],"derivedFrom":[subQ1,subQ0]});Q24=makeQuery(id+"F4.imprint","IMPRINT",FACE,{"disambiguationData":[TD([[makeQuery(id+"F4.imprint","IMPRINT",EDGE,{"disambiguationData":[TD([[subQ2,-1.0]])],"derivedFrom":subQ0}),-1.0]])]});}
            extrude(context, id + "F5", {"entities" : qUnion([Q0, Q1, Q2, Q3, Q4, Q5, Q6, Q7, Q8, Q9, Q10, Q11, Q12, Q13, Q14, Q15, Q16, Q17, Q18, Q19, Q20, Q21, Q22, Q23, Q24]), "operationType" : NewBodyOperationType.REMOVE, "oppositeDirection" : true, "depth" : 6.4 * mm, "offsetDistance" : 25 * mm});
        }
        {
            var Q0;
            Q0=makeQuery(id+"F5.boolean.opBoolean","COPY",EDGE,{"derivedFrom":makeQuery(id+"F5.opExtrude","CAP_EDGE",EDGE,{"disambiguationData":[OSD([sQuery(id+"F4.wireOp",EDGE,"E47")])],"isStart":false})});
            var Q1;
            Q1=makeQuery(id+"F5.boolean.opBoolean","COPY",EDGE,{"derivedFrom":makeQuery(id+"F5.opExtrude","CAP_EDGE",EDGE,{"disambiguationData":[OSD([sQuery(id+"F4.wireOp",EDGE,"E62.1.8")])],"isStart":false})});
            var Q2;
            Q2=makeQuery(id+"F5.boolean.opBoolean","COPY",EDGE,{"derivedFrom":makeQuery(id+"F5.opExtrude","CAP_EDGE",EDGE,{"disambiguationData":[OSD([sQuery(id+"F4.wireOp",EDGE,"E62.2.8")])],"isStart":false})});
            fillet(context, id + "F6", {"entities" : qUnion([Q0, Q1, Q2]), "tangentPropagation" : true, "radius" : 2.5 * mm, "defaultsChanged" : true, "vertexSettings" : [], "allowEdgeOverflow" : false});
        }
    });
